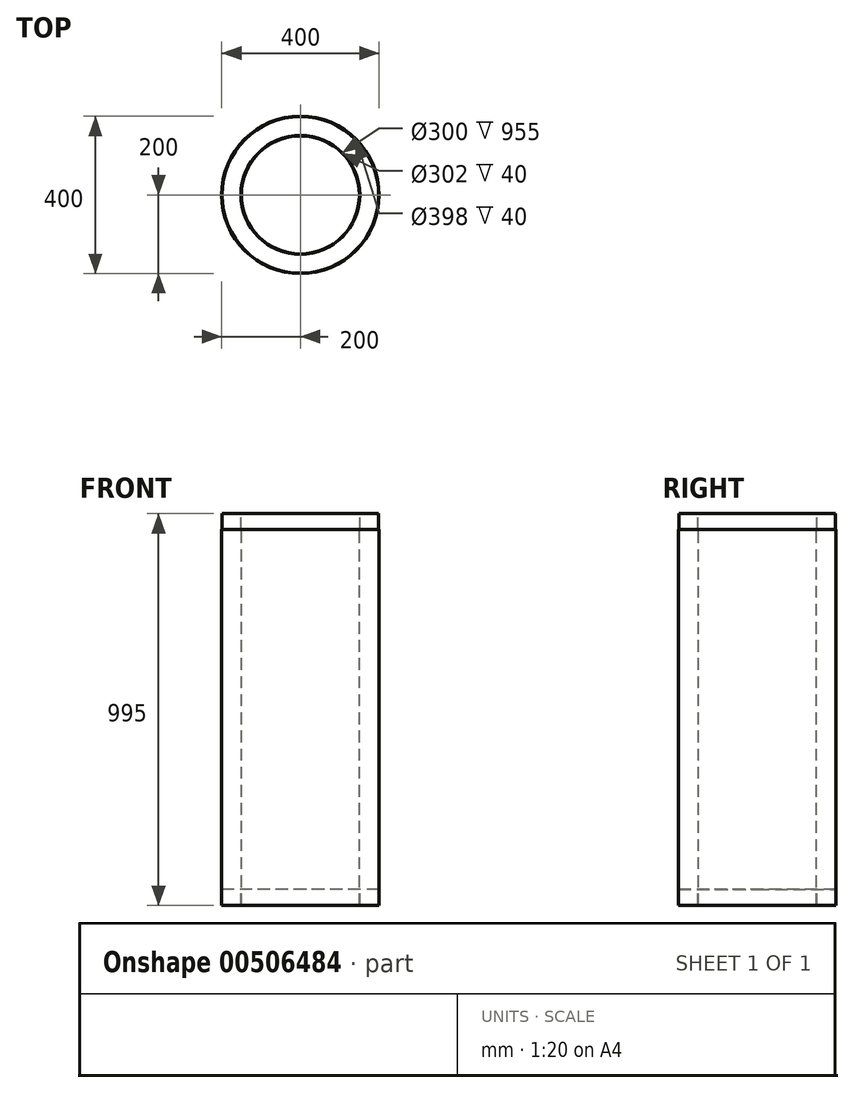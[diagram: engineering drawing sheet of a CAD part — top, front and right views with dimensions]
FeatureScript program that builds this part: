
annotation { "Feature Type Name" : "Feature", "Feature Type Description" : "" }
export const myFeature = defineFeature(function(context is Context, id is Id, definition is map)
    precondition{}
    {
        {
            var Q0;
            Q0=qCreatedBy(makeId("Front.planeOp"),FACE);
            var sketch = newSketch(context, id + "F0", { "sketchPlane" : qUnion([Q0])});
            skLineSegment(sketch, "E0", {"start": v(0, 452.89) * mm, "end": v(0, -450.9) * mm, "construction": true});
            skLineSegment(sketch, "E1", {"start": v(-150, -411.7) * mm, "end": v(-150, 543.3) * mm});
            skLineSegment(sketch, "E2", {"start": v(-150, 543.3) * mm, "end": v(-151, 543.3) * mm});
            skLineSegment(sketch, "E3", {"start": v(-151, 543.3) * mm, "end": v(-151, 583.3) * mm});
            skLineSegment(sketch, "E4", {"start": v(-151, 583.3) * mm, "end": v(-199, 583.3) * mm});
            skLineSegment(sketch, "E5", {"start": v(-199, 583.3) * mm, "end": v(-199, 543.3) * mm});
            skLineSegment(sketch, "E6", {"start": v(-199, 543.3) * mm, "end": v(-200, 543.3) * mm});
            skLineSegment(sketch, "E7", {"start": v(-200, 543.3) * mm, "end": v(-200, -411.7) * mm});
            skLineSegment(sketch, "E8", {"start": v(-200, -411.7) * mm, "end": v(-199, -411.7) * mm});
            skLineSegment(sketch, "E9", {"start": v(-199, -411.7) * mm, "end": v(-199, -371.7) * mm});
            skLineSegment(sketch, "E10", {"start": v(-199, -371.7) * mm, "end": v(-151, -371.7) * mm});
            skLineSegment(sketch, "E11", {"start": v(-151, -371.7) * mm, "end": v(-151, -411.7) * mm});
            skLineSegment(sketch, "E12", {"start": v(-151, -411.7) * mm, "end": v(-150, -411.7) * mm});
            skSolve(sketch);
        }
        {
            var Q0;
            Q0=qSketchRegion(id+"F0",true);
            var Q1;
            Q1=sQuery(id+"F0.wireOp",EDGE,"E0");
            revolve(context, id + "F1", {"entities" : qUnion([Q0]), "axis" : qUnion([Q1]), "revolveType" : RevolveType.FULL});
        }
    });
